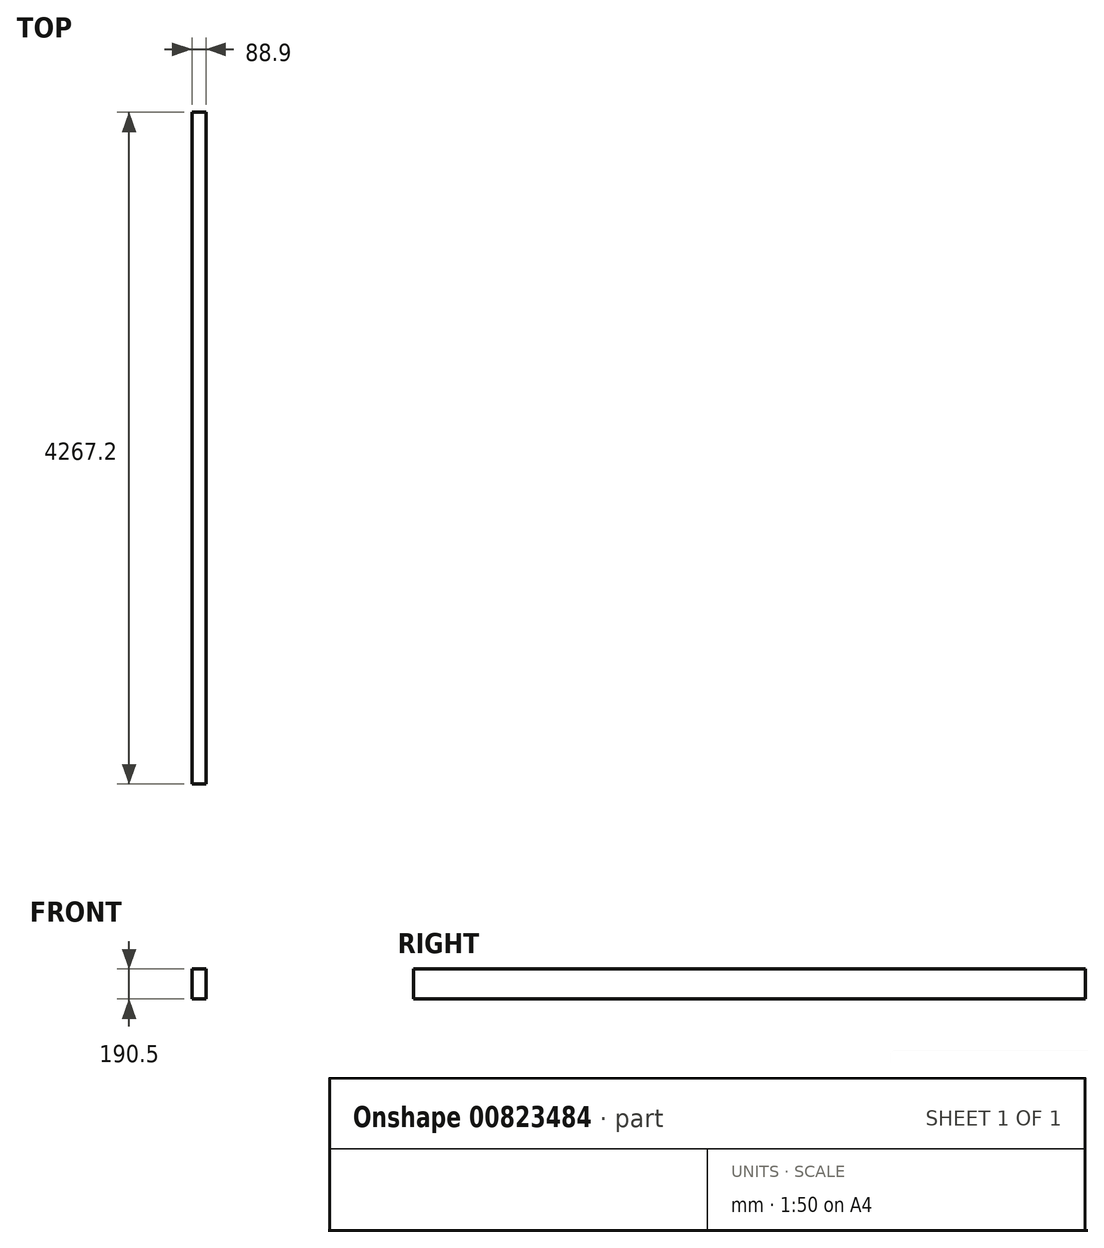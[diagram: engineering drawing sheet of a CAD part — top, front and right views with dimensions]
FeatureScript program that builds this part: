
annotation { "Feature Type Name" : "Feature", "Feature Type Description" : "" }
export const myFeature = defineFeature(function(context is Context, id is Id, definition is map)
    precondition{}
    {
        {
            var Q0;
            Q0=qCreatedBy(makeId("Front.planeOp"),FACE);
            var sketch = newSketch(context, id + "F0", { "sketchPlane" : qUnion([Q0])});
            skLineSegment(sketch, "E0.bottom", {"start": v(0, 0) * mm, "end": v(88.9, 0) * mm});
            skLineSegment(sketch, "E0.top", {"start": v(0, 190.5) * mm, "end": v(88.9, 190.5) * mm});
            skLineSegment(sketch, "E0.left", {"start": v(0, 0) * mm, "end": v(0, 190.5) * mm});
            skLineSegment(sketch, "E0.right", {"start": v(88.9, 0) * mm, "end": v(88.9, 190.5) * mm});
            skSolve(sketch);
        }
        {
            var Q0;
            Q0=qSketchRegion(id+"F0",true);
            extrude(context, id + "F1", {"entities" : qUnion([Q0]), "depth" : 4267.2 * mm, "offsetDistance" : 25.4 * mm});
        }
    });
